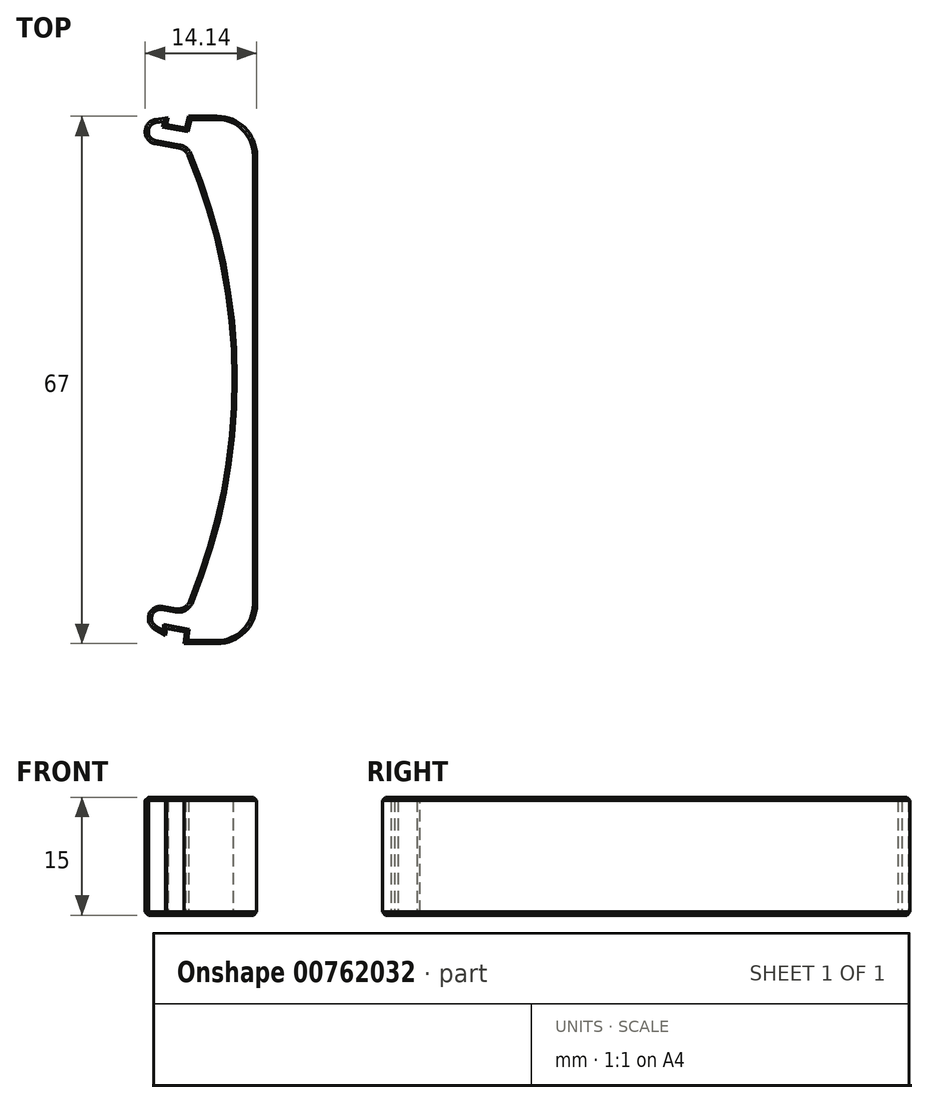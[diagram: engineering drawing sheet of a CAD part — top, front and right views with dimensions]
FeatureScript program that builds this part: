
annotation { "Feature Type Name" : "Feature", "Feature Type Description" : "" }
export const myFeature = defineFeature(function(context is Context, id is Id, definition is map)
    precondition{}
    {
        {
            var Q0;
            Q0=qCreatedBy(makeId("Top.planeOp"),FACE);
            var sketch = newSketch(context, id + "F0", { "sketchPlane" : qUnion([Q0])});
            skLineSegment(sketch, "E0.bottom", {"start": v(0, 33.5) * mm, "end": v(-9, 33.5) * mm});
            skLineSegment(sketch, "E0.top", {"start": v(0, -33.5) * mm, "end": v(-9, -33.5) * mm});
            skLineSegment(sketch, "E0.left", {"start": v(0, 33.5) * mm, "end": v(0, -33.5) * mm});
            skLineSegment(sketch, "E0.right", {"start": v(-9, 32) * mm, "end": v(-9, -33.5) * mm});
            skPoint(sketch, "E0.middle", {"position": v(-4.5, 0) * mm});
            skLineSegment(sketch, "E1", {"start": v(-9, 32) * mm, "end": v(0, 32) * mm});
            skLineSegment(sketch, "E2", {"start": v(-9, 29.3) * mm, "end": v(0, 29.3) * mm});
            skLineSegment(sketch, "E3.MirrorCS", {"start": v(-9, -29.3) * mm, "end": v(0, -29.3) * mm});
            skLineSegment(sketch, "E4.MirrorCS", {"start": v(-9, -32) * mm, "end": v(0, -32) * mm});
            skArc(sketch, "E5", {"start": v(-9, -29.3) * mm, "mid": v(-2.97, 0) * mm, "end": v(-9, 29.3) * mm});
            skLineSegment(sketch, "E6", {"start": v(-9, 32) * mm, "end": v(-9, 33.5) * mm});
            skPoint(sketch, "E7.orphan", {"position": v(-9, 33.5) * mm});
            skLineSegment(sketch, "E8", {"start": v(-9, -32) * mm, "end": v(-13.92, -31.1) * mm});
            skLineSegment(sketch, "E9", {"start": v(-9, 32) * mm, "end": v(-13.92, 32.9) * mm});
            skLineSegment(sketch, "E10", {"start": v(-13.92, -31.1) * mm, "end": v(-13.44, -28.48) * mm});
            skLineSegment(sketch, "E11", {"start": v(-9, -29.3) * mm, "end": v(-13.44, -28.48) * mm});
            skLineSegment(sketch, "E12", {"start": v(-13.92, 32.9) * mm, "end": v(-14.4, 30.3) * mm});
            skLineSegment(sketch, "E13", {"start": v(-9, 29.3) * mm, "end": v(-14.4, 30.3) * mm});
            skLineSegment(sketch, "E14", {"start": v(-13.92, -31.1) * mm, "end": v(-11.58, -32.44) * mm});
            skLineSegment(sketch, "E15", {"start": v(-11.58, -32.44) * mm, "end": v(-11.46, -31.55) * mm});
            skLineSegment(sketch, "E16", {"start": v(-13.92, 32.9) * mm, "end": v(-11.25, 33.33) * mm});
            skLineSegment(sketch, "E17", {"start": v(-11.25, 33.33) * mm, "end": v(-11.46, 32.45) * mm});
            skLineSegment(sketch, "E18", {"start": v(-9, 32) * mm, "end": v(-8.64, 33.5) * mm});
            skLineSegment(sketch, "E19", {"start": v(-9, -32) * mm, "end": v(-9.2, -33.5) * mm});
            skLineSegment(sketch, "E20", {"start": v(-9.2, -33.5) * mm, "end": v(-9, -33.5) * mm});
            skSolve(sketch);
        }
        {
            var Q0;
            {var subQ0=sQuery(id+"F0.wireOp",EDGE,"E10");Q0=makeQuery(id+"F0.imprint","IMPRINT",FACE,{"disambiguationData":[TD([[makeQuery(id+"F0.imprint","IMPRINT",EDGE,{"derivedFrom":subQ0}),-1.0]])]});}
            var Q1;
            {var subQ0=sQuery(id+"F0.wireOp",EDGE,"E3.MirrorCS");Q1=makeQuery(id+"F0.imprint","IMPRINT",FACE,{"disambiguationData":[TD([[makeQuery(id+"F0.imprint","IMPRINT",EDGE,{"derivedFrom":subQ0}),-1.0]])]});}
            var Q2;
            {var subQ2=sQuery(id+"F0.wireOp",EDGE,"E19");Q2=makeQuery(id+"F0.imprint","IMPRINT",FACE,{"disambiguationData":[TD([[makeQuery(id+"F0.imprint","IMPRINT",EDGE,{"derivedFrom":subQ2}),1.0]])]});}
            var Q3;
            {var subQ0=sQuery(id+"F0.wireOp",EDGE,"E0.top");Q3=makeQuery(id+"F0.imprint","IMPRINT",FACE,{"disambiguationData":[TD([[makeQuery(id+"F0.imprint","IMPRINT",EDGE,{"derivedFrom":subQ0}),-1.0]])]});}
            var Q4;
            {var subQ0=sQuery(id+"F0.wireOp",EDGE,"E14");Q4=makeQuery(id+"F0.imprint","IMPRINT",FACE,{"disambiguationData":[TD([[makeQuery(id+"F0.imprint","IMPRINT",EDGE,{"derivedFrom":subQ0}),1.0]])]});}
            var Q5;
            {var subQ0=sQuery(id+"F0.wireOp",EDGE,"E2");Q5=makeQuery(id+"F0.imprint","IMPRINT",FACE,{"disambiguationData":[TD([[makeQuery(id+"F0.imprint","IMPRINT",EDGE,{"derivedFrom":subQ0}),-1.0]])]});}
            var Q6;
            {var subQ0=sQuery(id+"F0.wireOp",EDGE,"E1");Q6=makeQuery(id+"F0.imprint","IMPRINT",FACE,{"disambiguationData":[TD([[makeQuery(id+"F0.imprint","IMPRINT",EDGE,{"derivedFrom":subQ0}),-1.0]])]});}
            var Q7;
            {var subQ4=sQuery(id+"F0.wireOp",EDGE,"E1");Q7=makeQuery(id+"F0.imprint","IMPRINT",FACE,{"disambiguationData":[TD([[makeQuery(id+"F0.imprint","IMPRINT",EDGE,{"derivedFrom":subQ4}),1.0]])]});}
            var Q8;
            {var subQ0=sQuery(id+"F0.wireOp",EDGE,"E12");Q8=makeQuery(id+"F0.imprint","IMPRINT",FACE,{"disambiguationData":[TD([[makeQuery(id+"F0.imprint","IMPRINT",EDGE,{"derivedFrom":subQ0}),1.0]])]});}
            var Q9;
            {var subQ0=sQuery(id+"F0.wireOp",EDGE,"E16");Q9=makeQuery(id+"F0.imprint","IMPRINT",FACE,{"disambiguationData":[TD([[makeQuery(id+"F0.imprint","IMPRINT",EDGE,{"derivedFrom":subQ0}),-1.0]])]});}
            extrude(context, id + "F1", {"entities" : qUnion([Q0, Q1, Q2, Q3, Q4, Q5, Q6, Q7, Q8, Q9]), "depth" : 15 * mm, "offsetDistance" : 25 * mm});
        }
        {
            var Q0;
            Q0=makeQuery(id+"F1.opExtrude","SWEPT_EDGE",EDGE,{"disambiguationData":[OSD([sQuery(id+"F0.wireOp",EDGE,"E12"),sQuery(id+"F0.wireOp",EDGE,"E13")])]});
            var Q1;
            Q1=makeQuery(id+"F1.opExtrude","SWEPT_EDGE",EDGE,{"disambiguationData":[OSD([sQuery(id+"F0.wireOp",EDGE,"E0.right"),sQuery(id+"F0.wireOp",EDGE,"E2"),sQuery(id+"F0.wireOp",EDGE,"E5"),sQuery(id+"F0.wireOp",EDGE,"E13")])]});
            var Q2;
            Q2=makeQuery(id+"F1.opExtrude","SWEPT_EDGE",EDGE,{"disambiguationData":[OSD([sQuery(id+"F0.wireOp",EDGE,"E10"),sQuery(id+"F0.wireOp",EDGE,"E11")])]});
            var Q3;
            Q3=makeQuery(id+"F1.opExtrude","SWEPT_EDGE",EDGE,{"disambiguationData":[OSD([sQuery(id+"F0.wireOp",EDGE,"E0.right"),sQuery(id+"F0.wireOp",EDGE,"E3.MirrorCS"),sQuery(id+"F0.wireOp",EDGE,"E5"),sQuery(id+"F0.wireOp",EDGE,"E11")])]});
            var Q4;
            Q4=makeQuery(id+"F1.opExtrude","SWEPT_EDGE",EDGE,{"disambiguationData":[OSD([sQuery(id+"F0.wireOp",EDGE,"E8"),sQuery(id+"F0.wireOp",EDGE,"E10"),sQuery(id+"F0.wireOp",EDGE,"E14")])]});
            var Q5;
            Q5=makeQuery(id+"F1.opExtrude","SWEPT_EDGE",EDGE,{"disambiguationData":[OSD([sQuery(id+"F0.wireOp",EDGE,"E9"),sQuery(id+"F0.wireOp",EDGE,"E12"),sQuery(id+"F0.wireOp",EDGE,"E16")])]});
            fillet(context, id + "F2", {"entities" : qUnion([Q0, Q1, Q2, Q3, Q4, Q5]), "radius" : 1.55 * mm, "tangentPropagation" : true, "allowEdgeOverflow" : false});
        }
        {
            var Q0;
            Q0=makeQuery(id+"F1.opExtrude","SWEPT_EDGE",EDGE,{"disambiguationData":[OSD([sQuery(id+"F0.wireOp",EDGE,"E0.bottom"),sQuery(id+"F0.wireOp",EDGE,"E0.left")])]});
            var Q1;
            Q1=makeQuery(id+"F1.opExtrude","SWEPT_EDGE",EDGE,{"disambiguationData":[OSD([sQuery(id+"F0.wireOp",EDGE,"E0.top"),sQuery(id+"F0.wireOp",EDGE,"E0.left")])]});
            fillet(context, id + "F3", {"entities" : qUnion([Q0, Q1]), "radius" : 5 * mm, "tangentPropagation" : true, "allowEdgeOverflow" : false});
        }
        {
            var Q0;
            Q0=makeQuery(id+"F1.opExtrude","CAP_FACE",FACE,{"disambiguationData":[OSD([sQuery(id+"F0.wireOp",EDGE,"E0.bottom"),sQuery(id+"F0.wireOp",EDGE,"E0.top"),sQuery(id+"F0.wireOp",EDGE,"E0.left"),sQuery(id+"F0.wireOp",EDGE,"E5"),sQuery(id+"F0.wireOp",EDGE,"E8"),sQuery(id+"F0.wireOp",EDGE,"E9"),sQuery(id+"F0.wireOp",EDGE,"E10"),sQuery(id+"F0.wireOp",EDGE,"E11"),sQuery(id+"F0.wireOp",EDGE,"E12"),sQuery(id+"F0.wireOp",EDGE,"E13"),sQuery(id+"F0.wireOp",EDGE,"E14"),sQuery(id+"F0.wireOp",EDGE,"E15"),sQuery(id+"F0.wireOp",EDGE,"E16"),sQuery(id+"F0.wireOp",EDGE,"E17"),sQuery(id+"F0.wireOp",EDGE,"E18"),sQuery(id+"F0.wireOp",EDGE,"E19"),sQuery(id+"F0.wireOp",EDGE,"E20")])],"isStart":false});
            var Q1;
            Q1=makeQuery(id+"F1.opExtrude","CAP_FACE",FACE,{"disambiguationData":[OSD([sQuery(id+"F0.wireOp",EDGE,"E0.bottom"),sQuery(id+"F0.wireOp",EDGE,"E0.top"),sQuery(id+"F0.wireOp",EDGE,"E0.left"),sQuery(id+"F0.wireOp",EDGE,"E5"),sQuery(id+"F0.wireOp",EDGE,"E8"),sQuery(id+"F0.wireOp",EDGE,"E9"),sQuery(id+"F0.wireOp",EDGE,"E10"),sQuery(id+"F0.wireOp",EDGE,"E11"),sQuery(id+"F0.wireOp",EDGE,"E12"),sQuery(id+"F0.wireOp",EDGE,"E13"),sQuery(id+"F0.wireOp",EDGE,"E14"),sQuery(id+"F0.wireOp",EDGE,"E15"),sQuery(id+"F0.wireOp",EDGE,"E16"),sQuery(id+"F0.wireOp",EDGE,"E17"),sQuery(id+"F0.wireOp",EDGE,"E18"),sQuery(id+"F0.wireOp",EDGE,"E19"),sQuery(id+"F0.wireOp",EDGE,"E20")])],"isStart":true});
            chamfer(context, id + "F4", {"entities" : qUnion([Q0, Q1]), "width" : 0.4 * mm, "tangentPropagation" : true});
        }
    });
